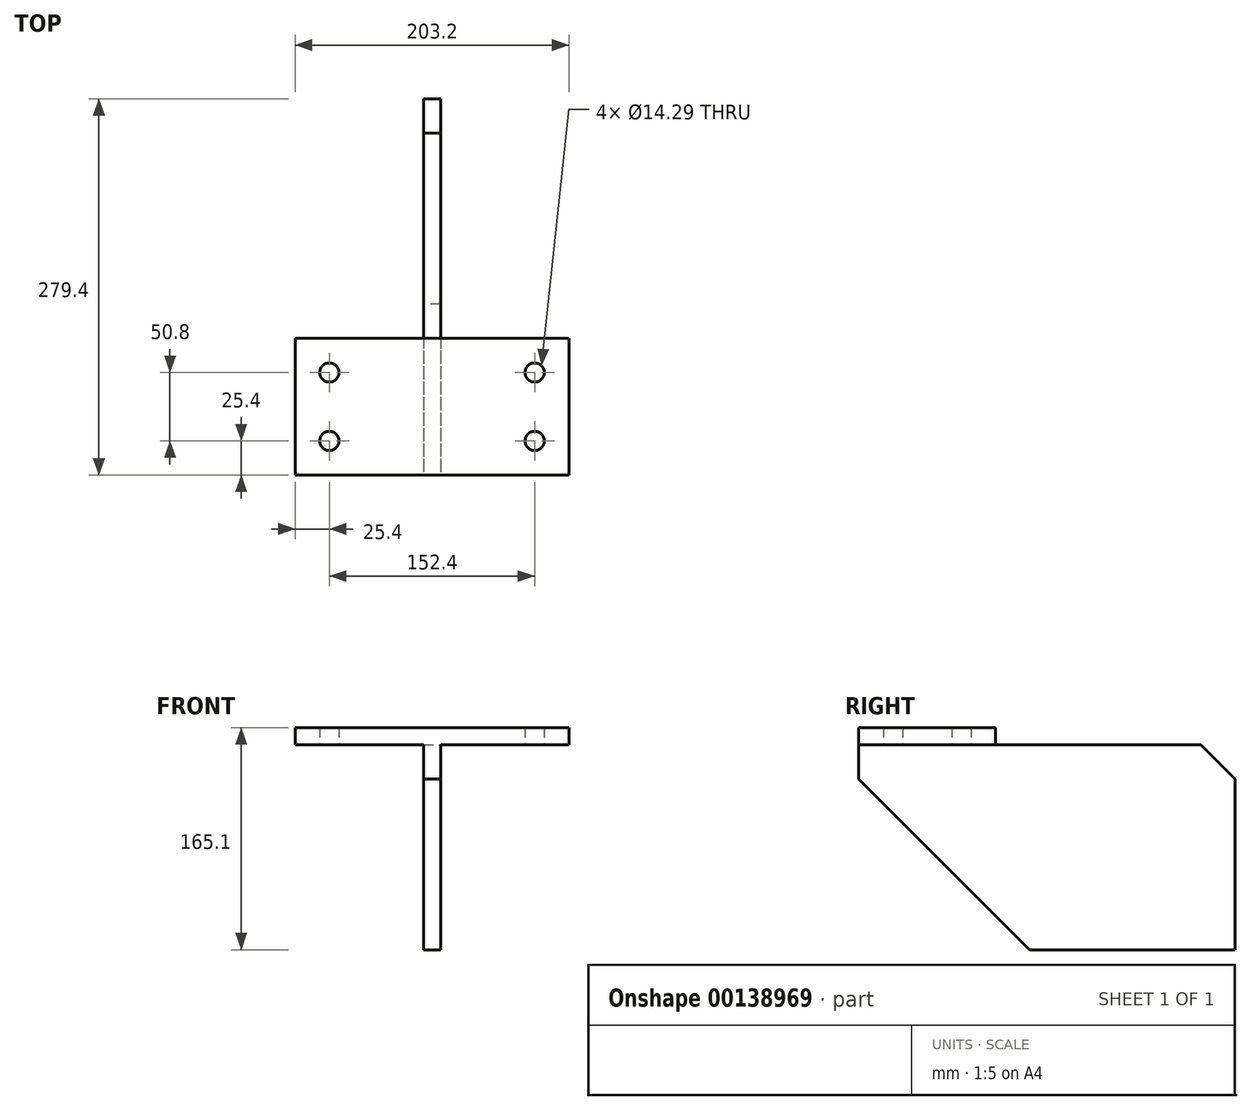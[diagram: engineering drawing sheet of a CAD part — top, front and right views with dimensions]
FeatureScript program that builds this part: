
annotation { "Feature Type Name" : "Feature", "Feature Type Description" : "" }
export const myFeature = defineFeature(function(context is Context, id is Id, definition is map)
    precondition{}
    {
        {
            var Q0;
            Q0=qCreatedBy(makeId("Top.planeOp"),FACE);
            var sketch = newSketch(context, id + "F0", { "sketchPlane" : qUnion([Q0])});
            skLineSegment(sketch, "E0.bottom", {"start": v(-101.6, 50.8) * mm, "end": v(101.6, 50.8) * mm});
            skLineSegment(sketch, "E0.top", {"start": v(-101.6, -50.8) * mm, "end": v(101.6, -50.8) * mm});
            skLineSegment(sketch, "E0.left", {"start": v(-101.6, 50.8) * mm, "end": v(-101.6, -50.8) * mm});
            skLineSegment(sketch, "E0.right", {"start": v(101.6, 50.8) * mm, "end": v(101.6, -50.8) * mm});
            skPoint(sketch, "E0.middle", {"position": v(0, 0) * mm});
            skLineSegment(sketch, "E1.bottom", {"start": v(-76.2, 25.4) * mm, "end": v(76.2, 25.4) * mm, "construction": true});
            skLineSegment(sketch, "E1.top", {"start": v(-76.2, -25.4) * mm, "end": v(76.2, -25.4) * mm, "construction": true});
            skLineSegment(sketch, "E1.left", {"start": v(-76.2, 25.4) * mm, "end": v(-76.2, -25.4) * mm, "construction": true});
            skLineSegment(sketch, "E1.right", {"start": v(76.2, 25.4) * mm, "end": v(76.2, -25.4) * mm, "construction": true});
            skCircle(sketch, "E2", {"center": v(-76.2, 25.4) * mm, "radius": 7.14 * mm});
            skCircle(sketch, "E3.0.1.0", {"center": v(-76.2, -25.4) * mm, "radius": 7.14 * mm});
            skCircle(sketch, "E3.1.0.0", {"center": v(76.2, 25.4) * mm, "radius": 7.14 * mm});
            skCircle(sketch, "E3.1.1.0", {"center": v(76.2, -25.4) * mm, "radius": 7.14 * mm});
            skSolve(sketch);
        }
        {
            var Q0;
            Q0 = qSketchRegion(id + "F0", true);
            extrude(context, id + "F1", {"entities" : qUnion([Q0]), "depth" : 12.7 * mm});
        }
        {
            var Q0;
            Q0=makeQuery(id+"F1.opExtrude","CAP_FACE",FACE,{"disambiguationData":[OSD([sQuery(id+"F0.wireOp",EDGE,"E0.bottom"),sQuery(id+"F0.wireOp",EDGE,"E0.top"),sQuery(id+"F0.wireOp",EDGE,"E0.left"),sQuery(id+"F0.wireOp",EDGE,"E0.right"),sQuery(id+"F0.wireOp",EDGE,"E2"),sQuery(id+"F0.wireOp",EDGE,"E3.0.1.0"),sQuery(id+"F0.wireOp",EDGE,"E3.1.0.0"),sQuery(id+"F0.wireOp",EDGE,"E3.1.1.0")])],"isStart":true});
            var sketch = newSketch(context, id + "F2", { "sketchPlane" : qUnion([Q0])});
            skLineSegment(sketch, "E4", {"start": v(0, 50.8) * mm, "end": v(0, -228.6) * mm, "construction": true});
            skPoint(sketch, "E4.endSnap0", {"position": v(0, -50.8) * mm});
            skLineSegment(sketch, "E5", {"start": v(0, -228.6) * mm, "end": v(-6.35, -228.6) * mm, "construction": true});
            skLineSegment(sketch, "E6.bottom", {"start": v(-6.35, -228.6) * mm, "end": v(6.35, -228.6) * mm});
            skLineSegment(sketch, "E6.top", {"start": v(-6.35, 50.8) * mm, "end": v(6.35, 50.8) * mm});
            skLineSegment(sketch, "E6.left", {"start": v(-6.35, -228.6) * mm, "end": v(-6.35, 50.8) * mm});
            skLineSegment(sketch, "E6.right", {"start": v(6.35, -228.6) * mm, "end": v(6.35, 50.8) * mm});
            skSolve(sketch);
        }
        {
            var Q0;
            Q0 = qSketchRegion(id + "F2", true);
            extrude(context, id + "F3", {"entities" : qUnion([Q0]), "operationType" : NewBodyOperationType.ADD, "depth" : 152.4 * mm});
        }
        {
            var Q0;
            Q0=makeQuery(id+"F3.opExtrude","SWEPT_FACE",FACE,{"disambiguationData":[OSD([sQuery(id+"F2.wireOp",EDGE,"E6.left")])]});
            var sketch = newSketch(context, id + "F4", { "sketchPlane" : qUnion([Q0])});
            skLineSegment(sketch, "E7.0", {"start": v(-50.8, 0) * mm, "end": v(50.8, 0) * mm, "construction": true});
            skLineSegment(sketch, "E8.0", {"start": v(-228.6, -152.4) * mm, "end": v(-228.6, 0) * mm, "construction": true});
            skLineSegment(sketch, "E9.0", {"start": v(-50.8, -25.4) * mm, "end": v(50.8, -25.4) * mm, "construction": true});
            skLineSegment(sketch, "E10.0", {"start": v(-76.2, -152.4) * mm, "end": v(-76.2, 0) * mm, "construction": true});
            skLineSegment(sketch, "E11", {"start": v(-76.2, -152.4) * mm, "end": v(50.8, -25.4) * mm});
            skLineSegment(sketch, "E12", {"start": v(50.8, -25.4) * mm, "end": v(50.8, -152.4) * mm});
            skLineSegment(sketch, "E13", {"start": v(50.8, -152.4) * mm, "end": v(-76.2, -152.4) * mm});
            skSolve(sketch);
        }
        {
            var Q0;
            Q0 = qSketchRegion(id + "F4", true);
            extrude(context, id + "F5", {"entities" : qUnion([Q0]), "operationType" : NewBodyOperationType.REMOVE, "endBound" : BoundingType.THROUGH_ALL, "oppositeDirection" : true, "depth" : 25.4 * mm});
        }
        {
            var Q0;
            Q0=makeQuery(id+"F3.opExtrude","CAP_EDGE",EDGE,{"disambiguationData":[OSD([sQuery(id+"F2.wireOp",EDGE,"E6.bottom")])],"isStart":true});
            chamfer(context, id + "F6", {"entities" : qUnion([Q0]), "width" : 25.4 * mm, "tangentPropagation" : true});
        }
    });
